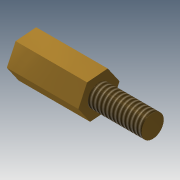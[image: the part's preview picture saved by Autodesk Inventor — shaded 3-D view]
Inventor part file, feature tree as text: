
AUTODESK INVENTOR PART (.ipt)
format: ipt  version: 2015 SP1 (Build 190203100, 203)  size: 103,936 bytes
history: native  units: mm
features: sketch x3, extrude x2, thread x1, hole x1
ambient origin geometry x8: Origin, YZ Plane, XZ Plane, XY Plane, X Axis, Y Axis, Z Axis, Center Point
bodies: Solid1 (feature_tree)
feature tree (7):
  extrude  "Extrusion1"  Depth=8.0mm TaperAngle=0.0deg
  extrude  "Extrusion2"  Depth=6.0mm TaperAngle=0.0deg
  thread  "Thread1"  [1 undecoded]
  hole  "Hole1"  [1 undecoded]
  sketch  "Sketch1"  dims[d0=2.0mm d1=8.0mm d2=0.0mm]
  sketch  "Sketch2"  dims[d3=2.5mm d4=6.0mm d5=0.0mm d6=10.0mm d7=0.0mm]
  sketch  "Sketch3"  dims[d8=2.013mm d9=6.0mm d10=4.0mm d11=2.0mm d12=90.0deg d13=5.0mm d14=20.594885mm]
note: 2 required parameter values undecoded (feature->parameter linkage not recoverable at this tier; creation-order binding heuristic only, values carry confidence <= 0.55)
